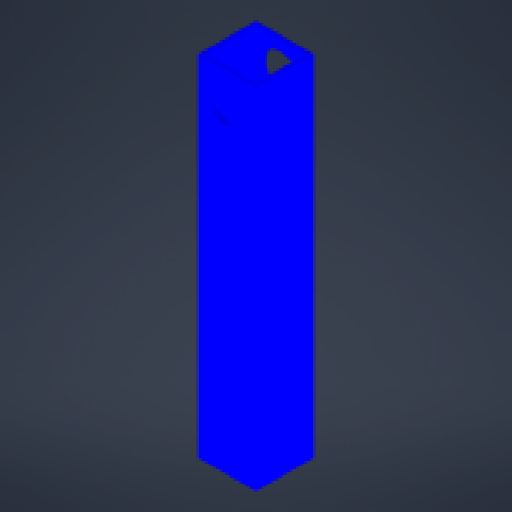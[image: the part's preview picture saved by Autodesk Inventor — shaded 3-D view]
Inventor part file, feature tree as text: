
AUTODESK INVENTOR PART (.ipt)
format: ipt  version: 2024 (Build 280153000, 153)  size: 150,528 bytes
history: native  units: mm
features: extrude x2, sketch x2, other x1
ambient origin geometry x8: Origin, YZ Plane, XZ Plane, XY Plane, X Axis, Y Axis, Z Axis, Center Point
bodies: Body1 (feature_tree)
feature tree (5):
  other  "Твердое тело1"
  extrude  "Выдавливание1"  Depth=1.5mm
  extrude  "Выдавливание2"  Depth=20.0mm
  sketch  "Эскиз1"
  sketch  "Эскиз2"
